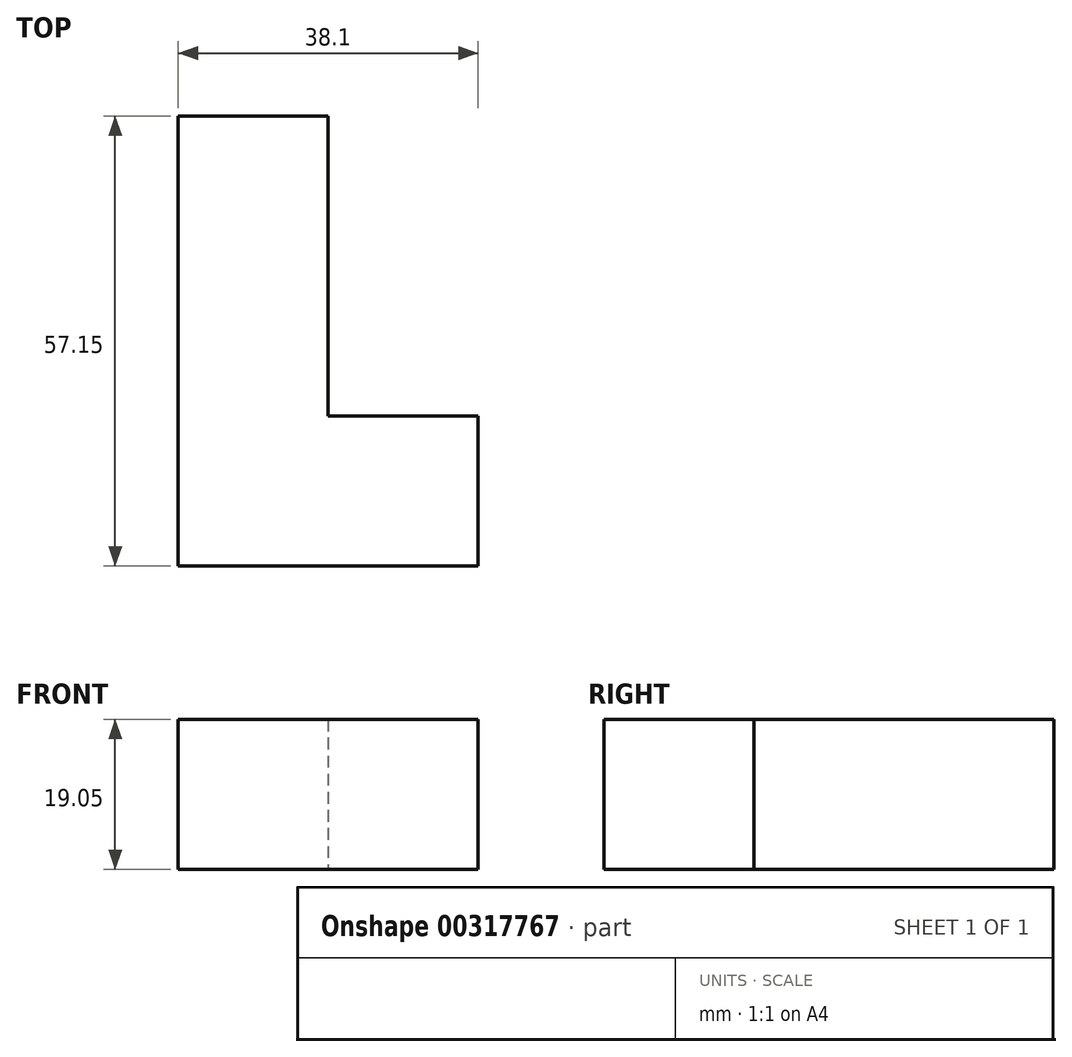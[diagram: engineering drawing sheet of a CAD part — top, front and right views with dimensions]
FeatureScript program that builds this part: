
annotation { "Feature Type Name" : "Feature", "Feature Type Description" : "" }
export const myFeature = defineFeature(function(context is Context, id is Id, definition is map)
    precondition{}
    {
        {
            var Q0;
            Q0=qCreatedBy(makeId("Top.planeOp"),FACE);
            var sketch = newSketch(context, id + "F0", { "sketchPlane" : qUnion([Q0])});
            skLineSegment(sketch, "E0.bottom", {"start": v(0, 0) * mm, "end": v(38.1, 0) * mm});
            skLineSegment(sketch, "E0.top", {"start": v(0, 19.05) * mm, "end": v(38.1, 19.05) * mm});
            skLineSegment(sketch, "E0.left", {"start": v(0, 0) * mm, "end": v(0, 19.05) * mm});
            skLineSegment(sketch, "E0.right", {"start": v(38.1, 0) * mm, "end": v(38.1, 19.05) * mm});
            skLineSegment(sketch, "E1.bottom", {"start": v(0, 0) * mm, "end": v(19.05, 0) * mm});
            skLineSegment(sketch, "E1.top", {"start": v(0, 57.15) * mm, "end": v(19.05, 57.15) * mm});
            skLineSegment(sketch, "E1.left", {"start": v(0, 0) * mm, "end": v(0, 57.15) * mm});
            skLineSegment(sketch, "E1.right", {"start": v(19.05, 0) * mm, "end": v(19.05, 57.15) * mm});
            skSolve(sketch);
        }
        {
            var Q0;
            {var subQ0=sQuery(id+"F0.wireOp",EDGE,"E0.bottom");Q0=makeQuery(id+"F0.imprint","IMPRINT",FACE,{"disambiguationData":[TD([[makeQuery(id+"F0.imprint","IMPRINT",EDGE,{"derivedFrom":subQ0}),1.0]])]});}
            var Q1;
            {var subQ5=sQuery(id+"F0.wireOp",EDGE,"E1.bottom");Q1=makeQuery(id+"F0.imprint","IMPRINT",FACE,{"disambiguationData":[TD([[makeQuery(id+"F0.imprint","IMPRINT",EDGE,{"derivedFrom":subQ5}),1.0]])]});}
            var Q2;
            {var subQ5=sQuery(id+"F0.wireOp",EDGE,"E1.top");Q2=makeQuery(id+"F0.imprint","IMPRINT",FACE,{"disambiguationData":[TD([[makeQuery(id+"F0.imprint","IMPRINT",EDGE,{"derivedFrom":subQ5}),-1.0]])]});}
            extrude(context, id + "F1", {"entities" : qUnion([Q0, Q1, Q2]), "depth" : 19.05 * mm});
        }
    });
